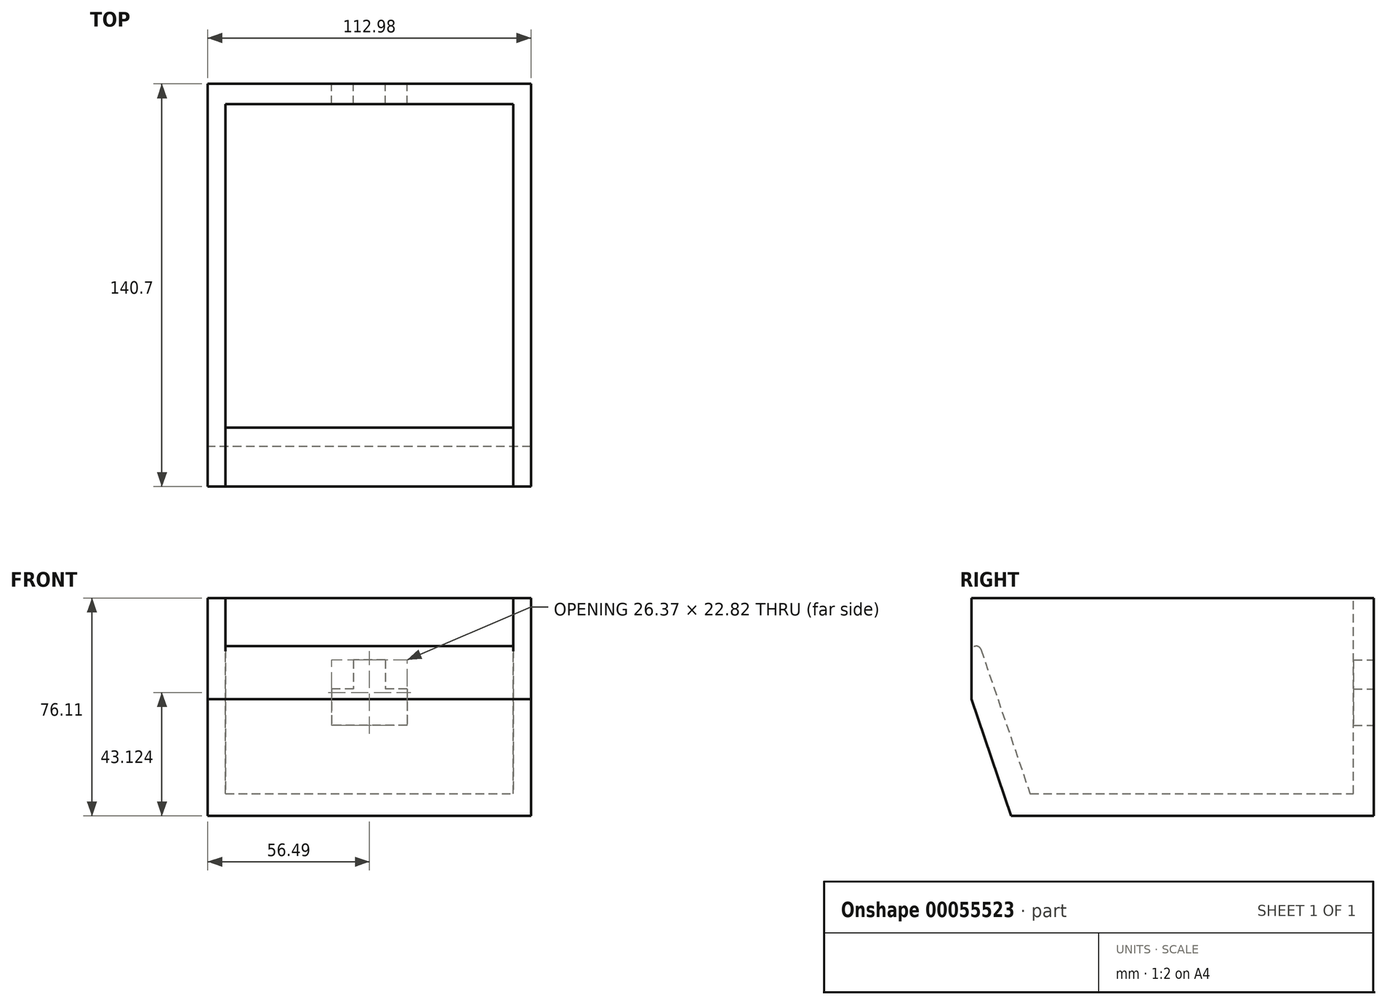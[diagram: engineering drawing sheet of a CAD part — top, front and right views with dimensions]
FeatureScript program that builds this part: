
annotation { "Feature Type Name" : "Feature", "Feature Type Description" : "" }
export const myFeature = defineFeature(function(context is Context, id is Id, definition is map)
    precondition{}
    {
        {
            var Q0;
            Q0=qCreatedBy(makeId("Right.planeOp"),FACE);
            var sketch = newSketch(context, id + "F0", { "sketchPlane" : qUnion([Q0])});
            skLineSegment(sketch, "E0", {"start": v(-76.37, 0) * mm, "end": v(-50.4, -76.11) * mm});
            skLineSegment(sketch, "E1", {"start": v(-50.4, -76.11) * mm, "end": v(76.37, -76.11) * mm});
            skLineSegment(sketch, "E2", {"start": v(76.37, -76.11) * mm, "end": v(76.37, 0) * mm});
            skLineSegment(sketch, "E3", {"start": v(76.37, 0) * mm, "end": v(-76.37, 0) * mm});
            skSolve(sketch);
        }
        {
            var Q0;
            Q0=makeQuery(id+"F0.imprint","IMPRINT",FACE,{"disambiguationData":[TD([[makeQuery(id+"F0.imprint","IMPRINT",EDGE,{"derivedFrom":sQuery(id+"F0.wireOp",EDGE,"E0")}),1.0]])]});
            var sketch = newSketch(context, id + "F1", { "sketchPlane" : qUnion([Q0])});
            skLineSegment(sketch, "E4", {"start": v(-67.06, 0) * mm, "end": v(-43.78, -68.35) * mm});
            skLineSegment(sketch, "E5", {"start": v(-43.78, -68.35) * mm, "end": v(69.24, -68.35) * mm});
            skLineSegment(sketch, "E6", {"start": v(69.24, -68.35) * mm, "end": v(69.24, 0) * mm});
            skLineSegment(sketch, "E7", {"start": v(69.24, 0) * mm, "end": v(-67.06, 0) * mm});
            skSolve(sketch);
        }
        {
            var Q0;
            Q0=makeQuery(id+"F0.imprint","IMPRINT",FACE,{"disambiguationData":[TD([[makeQuery(id+"F0.imprint","IMPRINT",EDGE,{"derivedFrom":sQuery(id+"F0.wireOp",EDGE,"E0")}),1.0]])]});
            extrude(context, id + "F2", {"entities" : qUnion([Q0]), "endBound" : BoundingType.SYMMETRIC, "depth" : 112.98 * mm});
        }
        {
            var Q0;
            Q0 = qSketchRegion(id + "F1", true);
            extrude(context, id + "F3", {"entities" : qUnion([Q0]), "operationType" : NewBodyOperationType.REMOVE, "endBound" : BoundingType.SYMMETRIC, "oppositeDirection" : true, "depth" : 100.6 * mm});
        }
        {
            var Q0;
            Q0=qCreatedBy(makeId("Right.planeOp"),FACE);
            var sketch = newSketch(context, id + "F4", { "sketchPlane" : qUnion([Q0])});
            skLineSegment(sketch, "E8.bottom", {"start": v(-66.94, 10.71) * mm, "end": v(-84.58, 10.71) * mm});
            skLineSegment(sketch, "E8.top", {"start": v(-66.94, -23.94) * mm, "end": v(-84.58, -23.94) * mm});
            skLineSegment(sketch, "E8.left", {"start": v(-66.94, 10.71) * mm, "end": v(-66.94, -23.94) * mm});
            skLineSegment(sketch, "E8.right", {"start": v(-84.58, 10.71) * mm, "end": v(-84.58, -23.94) * mm});
            skSolve(sketch);
        }
        {
            var Q0;
            Q0=makeQuery(id+"F4.imprint","IMPRINT",FACE,{"disambiguationData":[TD([[makeQuery(id+"F4.imprint","IMPRINT",EDGE,{"derivedFrom":sQuery(id+"F4.wireOp",EDGE,"E8.bottom")}),1.0]])]});
            extrude(context, id + "F5", {"entities" : qUnion([Q0]), "operationType" : NewBodyOperationType.REMOVE, "endBound" : BoundingType.SYMMETRIC, "oppositeDirection" : true, "depth" : 304.8 * mm});
        }
        {
            var Q0;
            Q0=qCreatedBy(makeId("Right.planeOp"),FACE);
            var sketch = newSketch(context, id + "F6", { "sketchPlane" : qUnion([Q0])});
            skLineSegment(sketch, "E9.bottom", {"start": v(-64.33, 5.04) * mm, "end": v(-72.52, 5.04) * mm});
            skLineSegment(sketch, "E9.top", {"start": v(-64.33, -35.6) * mm, "end": v(-72.52, -35.6) * mm});
            skLineSegment(sketch, "E9.left", {"start": v(-64.33, 5.04) * mm, "end": v(-64.33, -35.6) * mm});
            skLineSegment(sketch, "E9.right", {"start": v(-72.52, 5.04) * mm, "end": v(-72.52, -35.6) * mm});
            skSolve(sketch);
        }
        {
            var Q0;
            Q0=makeQuery(id+"F6.imprint","IMPRINT",FACE,{"disambiguationData":[TD([[makeQuery(id+"F6.imprint","IMPRINT",EDGE,{"derivedFrom":sQuery(id+"F6.wireOp",EDGE,"E9.bottom")}),1.0]])]});
            extrude(context, id + "F7", {"entities" : qUnion([Q0]), "operationType" : NewBodyOperationType.REMOVE, "endBound" : BoundingType.SYMMETRIC, "oppositeDirection" : true, "depth" : 304.8 * mm});
        }
        {
            var Q0;
            Q0=makeQuery(id+"F7.boolean.opBoolean","INTERSECT",EDGE,{"derivedFrom":[makeQuery(id+"F3.boolean.opBoolean","COPY",FACE,{"derivedFrom":makeQuery(id+"F3.opExtrude","SWEPT_FACE",FACE,{"disambiguationData":[OSD([sQuery(id+"F1.wireOp",EDGE,"E4")])]})}),makeQuery(id+"F7.opExtrude","SWEPT_FACE",FACE,{"disambiguationData":[OSD([sQuery(id+"F6.wireOp",EDGE,"E9.left")])]})]});
            fillet(context, id + "F8", {"entities" : qUnion([Q0]), "radius" : 1.74 * mm, "tangentPropagation" : true, "allowEdgeOverflow" : false});
        }
        {
            var Q0;
            Q0=makeQuery(id+"F2.opExtrude","SWEPT_FACE",FACE,{"disambiguationData":[OSD([sQuery(id+"F0.wireOp",EDGE,"E2")])]});
            var sketch = newSketch(context, id + "F9", { "sketchPlane" : qUnion([Q0])});
            skLineSegment(sketch, "E10.rect.bottom", {"start": v(-13.18, -31.72) * mm, "end": v(13.18, -31.72) * mm});
            skLineSegment(sketch, "E10.rect.top", {"start": v(-13.18, -44.4) * mm, "end": v(13.18, -44.4) * mm});
            skLineSegment(sketch, "E10.rect.left", {"start": v(-13.18, -31.72) * mm, "end": v(-13.18, -44.4) * mm});
            skLineSegment(sketch, "E10.rect.right", {"start": v(13.18, -31.72) * mm, "end": v(13.18, -44.4) * mm});
            skPoint(sketch, "E10.rect.middle", {"position": v(0, -38.06) * mm});
            skPoint(sketch, "E10.rect.middle.positionSnap0", {"position": v(-56.5, -38.06) * mm});
            skPoint(sketch, "E10.rect.centerSnap0", {"position": v(-56.5, -38.06) * mm});
            skLineSegment(sketch, "E11.rect.bottom", {"start": v(-5.58, -21.58) * mm, "end": v(5.58, -21.58) * mm});
            skLineSegment(sketch, "E11.rect.top", {"start": v(-5.58, -41.86) * mm, "end": v(5.58, -41.86) * mm});
            skLineSegment(sketch, "E11.rect.left", {"start": v(-5.58, -21.58) * mm, "end": v(-5.58, -41.86) * mm});
            skLineSegment(sketch, "E11.rect.right", {"start": v(5.58, -21.58) * mm, "end": v(5.58, -41.86) * mm});
            skPoint(sketch, "E11.rect.middle", {"position": v(0, -31.72) * mm});
            skSolve(sketch);
        }
        {
            var Q0;
            Q0=makeQuery(id+"F9.imprint","IMPRINT",FACE,{"disambiguationData":[TD([[makeQuery(id+"F9.imprint","IMPRINT",EDGE,{"derivedFrom":sQuery(id+"F9.wireOp",EDGE,"E10.rect.top")}),1.0]])]});
            var Q1;
            {var subQ5=sQuery(id+"F9.wireOp",EDGE,"E11.rect.bottom");Q1=makeQuery(id+"F9.imprint","IMPRINT",FACE,{"disambiguationData":[TD([[makeQuery(id+"F9.imprint","IMPRINT",EDGE,{"derivedFrom":subQ5}),-1.0]])]});}
            var Q2;
            {var subQ5=sQuery(id+"F9.wireOp",EDGE,"E11.rect.top");Q2=makeQuery(id+"F9.imprint","IMPRINT",FACE,{"disambiguationData":[TD([[makeQuery(id+"F9.imprint","IMPRINT",EDGE,{"derivedFrom":subQ5}),1.0]])]});}
            extrude(context, id + "F10", {"entities" : qUnion([Q0, Q1, Q2]), "operationType" : NewBodyOperationType.REMOVE, "oppositeDirection" : true, "depth" : 26.24 * mm});
        }
    });
